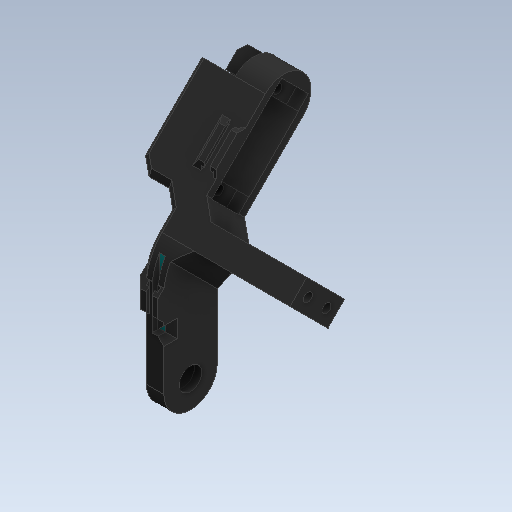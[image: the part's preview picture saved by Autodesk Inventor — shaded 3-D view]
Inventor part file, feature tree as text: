
AUTODESK INVENTOR PART (.ipt)
format: ipt  version: 2020 (Build 240168000, 168)  size: 433,664 bytes
history: native  units: in
note: dims shown in document units (in); Inventor stores cm internally (conversion verified against a paired STEP export)
features: sketch x26, other x7, plane x4
ambient origin geometry x8: Origin, YZ Plane, XZ Plane, XY Plane, X Axis, Y Axis, Z Axis, Center Point
bodies: Solid2 (feature_tree), Solid3 (feature_tree), Solid1 (feature_tree), Solid4 (feature_tree)
feature tree (37):
  other  "PatellaBot.ipt"
  other  "Solid1::PatellaBot.ipt"
  other  "Solid4::PatellaBot.ipt"
  other  "Solid5::PatellaBot.ipt"
  other  "Solid2::PatellaBot.ipt"
  other  "Solid3::PatellaBot.ipt"
  other  "TaggingFeature1"
  sketch  "Sketch1"  dims[d0=0.3937in]
  sketch  "Sketch2"
  sketch  "Sketch3"
  sketch  "Sketch4"
  sketch  "Sketch5"
  sketch  "Sketch12"
  sketch  "Sketch14"
  sketch  "Sketch15"
  sketch  "Sketch16"
  sketch  "Sketch17"
  sketch  "Sketch19"
  sketch  "Sketch22"
  sketch  "Sketch23"
  sketch  "Sketch25"
  sketch  "Sketch26"
  sketch  "Sketch27"
  sketch  "Sketch28"
  sketch  "Sketch32"
  sketch  "Sketch33"
  sketch  "Sketch39"
  sketch  "Sketch40"
  sketch  "Sketch46"
  sketch  "Sketch47"
  sketch  "Sketch48"
  sketch  "Sketch49"
  sketch  "Sketch50"
  plane  "Work Plane1"
  plane  "Work Plane2"
  plane  "Work Plane3"
  plane  "Work Plane4"
